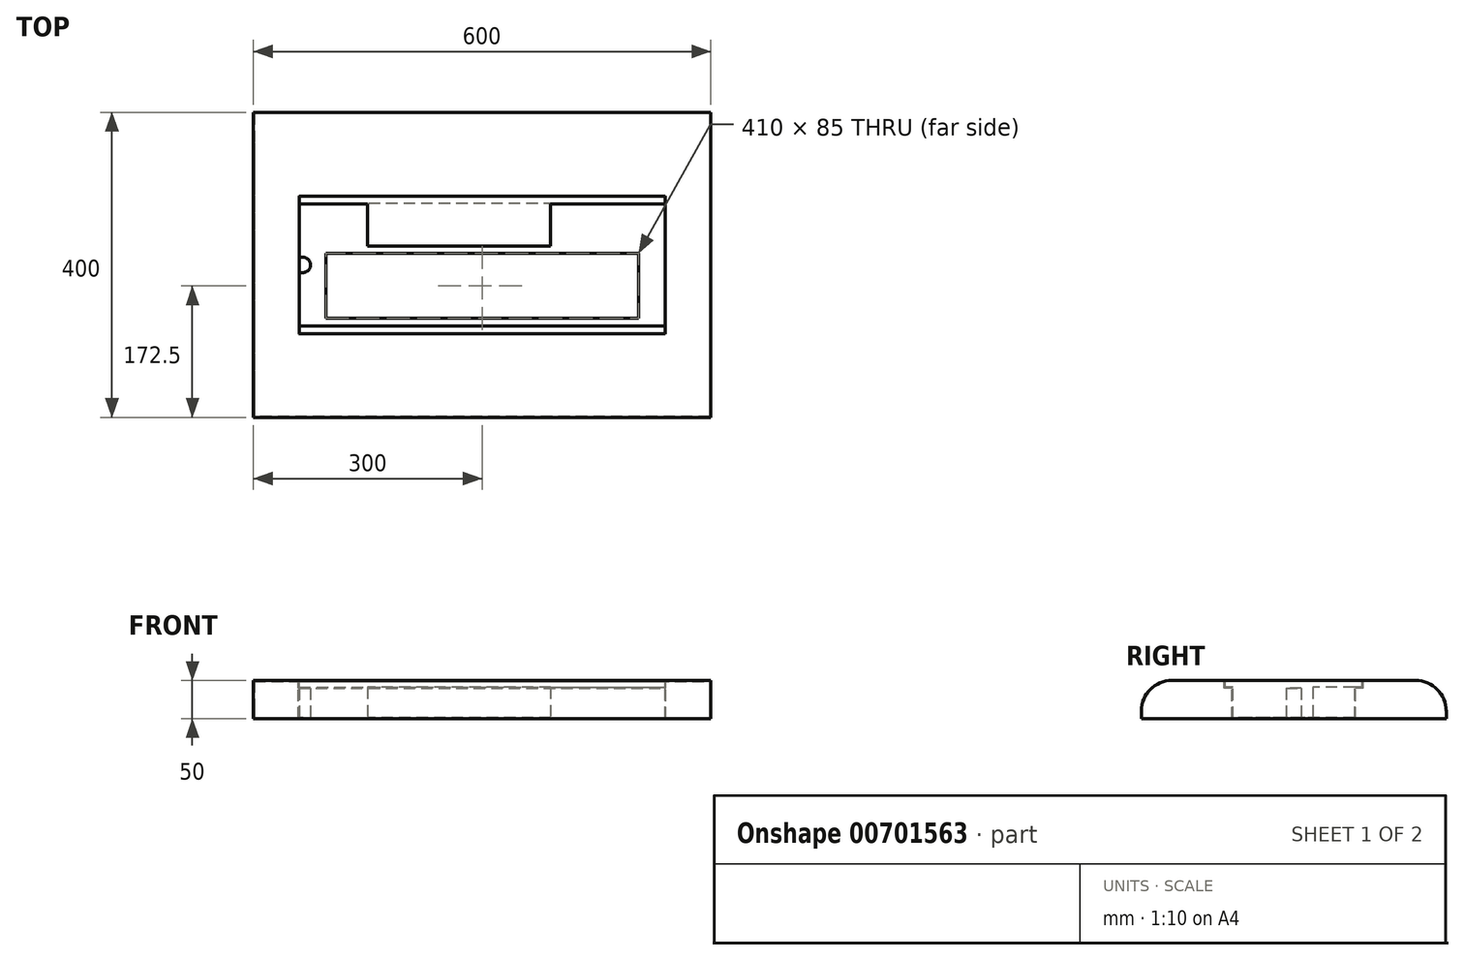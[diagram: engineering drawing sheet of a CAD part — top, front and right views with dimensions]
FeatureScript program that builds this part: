
annotation { "Feature Type Name" : "Feature", "Feature Type Description" : "" }
export const myFeature = defineFeature(function(context is Context, id is Id, definition is map)
    precondition{}
    {
        {
            var Q0;
            Q0=qCreatedBy(makeId("Top.planeOp"),FACE);
            var sketch = newSketch(context, id + "F0", { "sketchPlane" : qUnion([Q0])});
            skLineSegment(sketch, "E0.bottom", {"start": v(300, 200) * mm, "end": v(-300, 200) * mm});
            skLineSegment(sketch, "E0.top", {"start": v(300, -200) * mm, "end": v(-300, -200) * mm});
            skLineSegment(sketch, "E0.left", {"start": v(300, 200) * mm, "end": v(300, -200) * mm});
            skLineSegment(sketch, "E0.right", {"start": v(-300, 200) * mm, "end": v(-300, -200) * mm});
            skPoint(sketch, "E0.middle", {"position": v(0, 0) * mm});
            skSolve(sketch);
        }
        {
            var Q0;
            Q0=makeQuery(id+"F0.imprint","IMPRINT",FACE,{"disambiguationData":[TD([[makeQuery(id+"F0.imprint","IMPRINT",EDGE,{"derivedFrom":sQuery(id+"F0.wireOp",EDGE,"E0.bottom")}),1.0]])]});
            extrude(context, id + "F1", {"entities" : qUnion([Q0]), "depth" : 50 * mm, "offsetDistance" : 25 * mm});
        }
        {
            var Q0;
            Q0=makeQuery(id+"F1.opExtrude","CAP_EDGE",EDGE,{"disambiguationData":[OSD([sQuery(id+"F0.wireOp",EDGE,"E0.top")])],"isStart":false});
            var Q1;
            Q1=makeQuery(id+"F1.opExtrude","CAP_EDGE",EDGE,{"disambiguationData":[OSD([sQuery(id+"F0.wireOp",EDGE,"E0.bottom")])],"isStart":false});
            fillet(context, id + "F2", {"entities" : qUnion([Q0, Q1]), "radius" : 40 * mm, "tangentPropagation" : true, "allowEdgeOverflow" : false});
        }
        {
            var Q0;
            Q0=makeQuery(id+"F1.opExtrude","CAP_FACE",FACE,{"disambiguationData":[OSD([sQuery(id+"F0.wireOp",EDGE,"E0.bottom"),sQuery(id+"F0.wireOp",EDGE,"E0.top"),sQuery(id+"F0.wireOp",EDGE,"E0.left"),sQuery(id+"F0.wireOp",EDGE,"E0.right")])],"isStart":false});
            var sketch = newSketch(context, id + "F3", { "sketchPlane" : qUnion([Q0])});
            skLineSegment(sketch, "E1.bottom", {"start": v(-240, 80) * mm, "end": v(240, 80) * mm});
            skLineSegment(sketch, "E1.top", {"start": v(-240, -80) * mm, "end": v(240, -80) * mm});
            skLineSegment(sketch, "E1.left", {"start": v(-240, 80) * mm, "end": v(-240, -80) * mm});
            skLineSegment(sketch, "E1.right", {"start": v(240, 80) * mm, "end": v(240, -80) * mm});
            skPoint(sketch, "E1.middle", {"position": v(0, 0) * mm});
            skSolve(sketch);
        }
        {
            var Q0;
            Q0=makeQuery(id+"F3.imprint","IMPRINT",FACE,{"disambiguationData":[TD([[makeQuery(id+"F3.imprint","IMPRINT",EDGE,{"derivedFrom":sQuery(id+"F3.wireOp",EDGE,"E1.bottom")}),-1.0]])]});
            extrude(context, id + "F4", {"entities" : qUnion([Q0]), "operationType" : NewBodyOperationType.REMOVE, "oppositeDirection" : true, "depth" : 49 * mm, "offsetDistance" : 25 * mm});
        }
        {
            var Q0;
            Q0=makeQuery(id+"F1.opExtrude","CAP_FACE",FACE,{"disambiguationData":[OSD([sQuery(id+"F0.wireOp",EDGE,"E0.bottom"),sQuery(id+"F0.wireOp",EDGE,"E0.top"),sQuery(id+"F0.wireOp",EDGE,"E0.left"),sQuery(id+"F0.wireOp",EDGE,"E0.right")])],"isStart":false});
            var sketch = newSketch(context, id + "F5", { "sketchPlane" : qUnion([Q0])});
            skLineSegment(sketch, "E2.bottom", {"start": v(-240, 90) * mm, "end": v(240, 90) * mm});
            skLineSegment(sketch, "E2.top", {"start": v(-240, -90) * mm, "end": v(240, -90) * mm});
            skLineSegment(sketch, "E2.left", {"start": v(-240, 90) * mm, "end": v(-240, -90) * mm});
            skLineSegment(sketch, "E2.right", {"start": v(240, 90) * mm, "end": v(240, -90) * mm});
            skPoint(sketch, "E2.middle", {"position": v(0, 0) * mm});
            skSolve(sketch);
        }
        {
            var Q0;
            {var subQ0=sQuery(id+"F5.wireOp",EDGE,"E2.bottom");Q0=makeQuery(id+"F5.imprint","IMPRINT",FACE,{"disambiguationData":[TD([[makeQuery(id+"F5.imprint","IMPRINT",EDGE,{"derivedFrom":subQ0}),-1.0]])]});}
            var Q1;
            {var subQ0=sQuery(id+"F5.wireOp",EDGE,"E2.top");Q1=makeQuery(id+"F5.imprint","IMPRINT",FACE,{"disambiguationData":[TD([[makeQuery(id+"F5.imprint","IMPRINT",EDGE,{"derivedFrom":subQ0}),1.0]])]});}
            extrude(context, id + "F6", {"entities" : qUnion([Q0, Q1]), "operationType" : NewBodyOperationType.REMOVE, "oppositeDirection" : true, "depth" : 9 * mm, "offsetDistance" : 25 * mm});
        }
        {
            var Q0;
            Q0=makeQuery(id+"F1.opExtrude","CAP_FACE",FACE,{"disambiguationData":[OSD([sQuery(id+"F0.wireOp",EDGE,"E0.bottom"),sQuery(id+"F0.wireOp",EDGE,"E0.top"),sQuery(id+"F0.wireOp",EDGE,"E0.left"),sQuery(id+"F0.wireOp",EDGE,"E0.right")])],"isStart":true});
            shell(context, id + "F7", {"entities" : qUnion([Q0]), "thickness" : 1 * mm});
        }
        {
            var Q0;
            Q0=makeQuery(id+"F4.boolean.opBoolean","COPY",FACE,{"derivedFrom":makeQuery(id+"F4.opExtrude","CAP_FACE",FACE,{"disambiguationData":[OSD([sQuery(id+"F3.wireOp",EDGE,"E1.bottom"),sQuery(id+"F3.wireOp",EDGE,"E1.top"),sQuery(id+"F3.wireOp",EDGE,"E1.left"),sQuery(id+"F3.wireOp",EDGE,"E1.right")])],"isStart":false})});
            var sketch = newSketch(context, id + "F8", { "sketchPlane" : qUnion([Q0])});
            skLineSegment(sketch, "E3.bottom", {"start": v(-205, 15) * mm, "end": v(205, 15) * mm});
            skLineSegment(sketch, "E3.top", {"start": v(-205, -70) * mm, "end": v(205, -70) * mm});
            skLineSegment(sketch, "E3.left", {"start": v(-205, 15) * mm, "end": v(-205, -70) * mm});
            skLineSegment(sketch, "E3.right", {"start": v(205, 15) * mm, "end": v(205, -70) * mm});
            skPoint(sketch, "E3.middle", {"position": v(0, -27.5) * mm});
            skSolve(sketch);
        }
        {
            var Q0;
            Q0=makeQuery(id+"F8.imprint","IMPRINT",FACE,{"disambiguationData":[TD([[makeQuery(id+"F8.imprint","IMPRINT",EDGE,{"derivedFrom":sQuery(id+"F8.wireOp",EDGE,"E3.bottom")}),-1.0]])]});
            extrude(context, id + "F9", {"entities" : qUnion([Q0]), "operationType" : NewBodyOperationType.REMOVE, "endBound" : BoundingType.THROUGH_ALL, "oppositeDirection" : true, "depth" : 25 * mm, "offsetDistance" : 25 * mm});
        }
        {
            var Q0;
            Q0=makeQuery(id+"F4.boolean.opBoolean","COPY",FACE,{"derivedFrom":makeQuery(id+"F4.opExtrude","CAP_FACE",FACE,{"disambiguationData":[OSD([sQuery(id+"F3.wireOp",EDGE,"E1.bottom"),sQuery(id+"F3.wireOp",EDGE,"E1.top"),sQuery(id+"F3.wireOp",EDGE,"E1.left"),sQuery(id+"F3.wireOp",EDGE,"E1.right")])],"isStart":false})});
            var sketch = newSketch(context, id + "F10", { "sketchPlane" : qUnion([Q0])});
            skLineSegment(sketch, "E4.bottom", {"start": v(90, 80) * mm, "end": v(-150, 80) * mm});
            skLineSegment(sketch, "E4.top", {"start": v(90, 25) * mm, "end": v(-150, 25) * mm});
            skLineSegment(sketch, "E4.left", {"start": v(90, 80) * mm, "end": v(90, 25) * mm});
            skLineSegment(sketch, "E4.right", {"start": v(-150, 80) * mm, "end": v(-150, 25) * mm});
            skPoint(sketch, "E4.middle", {"position": v(-30, 52.5) * mm});
            skSolve(sketch);
        }
        {
            var Q0;
            Q0=makeQuery(id+"F10.imprint","IMPRINT",FACE,{"disambiguationData":[TD([[makeQuery(id+"F10.imprint","IMPRINT",EDGE,{"derivedFrom":sQuery(id+"F10.wireOp",EDGE,"E4.bottom")}),-1.0]])]});
            extrude(context, id + "F11", {"entities" : qUnion([Q0]), "operationType" : NewBodyOperationType.ADD, "depth" : 40 * mm, "offsetDistance" : 25 * mm});
        }
        {
            var Q0;
            Q0=makeQuery(id+"F4.boolean.opBoolean","COPY",FACE,{"derivedFrom":makeQuery(id+"F4.opExtrude","CAP_FACE",FACE,{"disambiguationData":[OSD([sQuery(id+"F3.wireOp",EDGE,"E1.bottom"),sQuery(id+"F3.wireOp",EDGE,"E1.top"),sQuery(id+"F3.wireOp",EDGE,"E1.left"),sQuery(id+"F3.wireOp",EDGE,"E1.right")])],"isStart":false})});
            var sketch = newSketch(context, id + "F12", { "sketchPlane" : qUnion([Q0])});
            skArc(sketch, "E5", {"start": v(-235, -10) * mm, "mid": v(-225, 0) * mm, "end": v(-235, 10) * mm});
            skLineSegment(sketch, "E6", {"start": v(-240, -10) * mm, "end": v(-235, -10) * mm});
            skLineSegment(sketch, "E7", {"start": v(-235, 10) * mm, "end": v(-240, 10) * mm});
            skLineSegment(sketch, "E8", {"start": v(-240, 10) * mm, "end": v(-240, -10) * mm});
            skSolve(sketch);
        }
        {
            var Q0;
            Q0=makeQuery(id+"F12.imprint","IMPRINT",FACE,{"disambiguationData":[TD([[makeQuery(id+"F12.imprint","IMPRINT",EDGE,{"derivedFrom":sQuery(id+"F12.wireOp",EDGE,"E5")}),1.0]])]});
            extrude(context, id + "F13", {"entities" : qUnion([Q0]), "operationType" : NewBodyOperationType.ADD, "depth" : 39 * mm, "offsetDistance" : 25 * mm});
        }
    });
